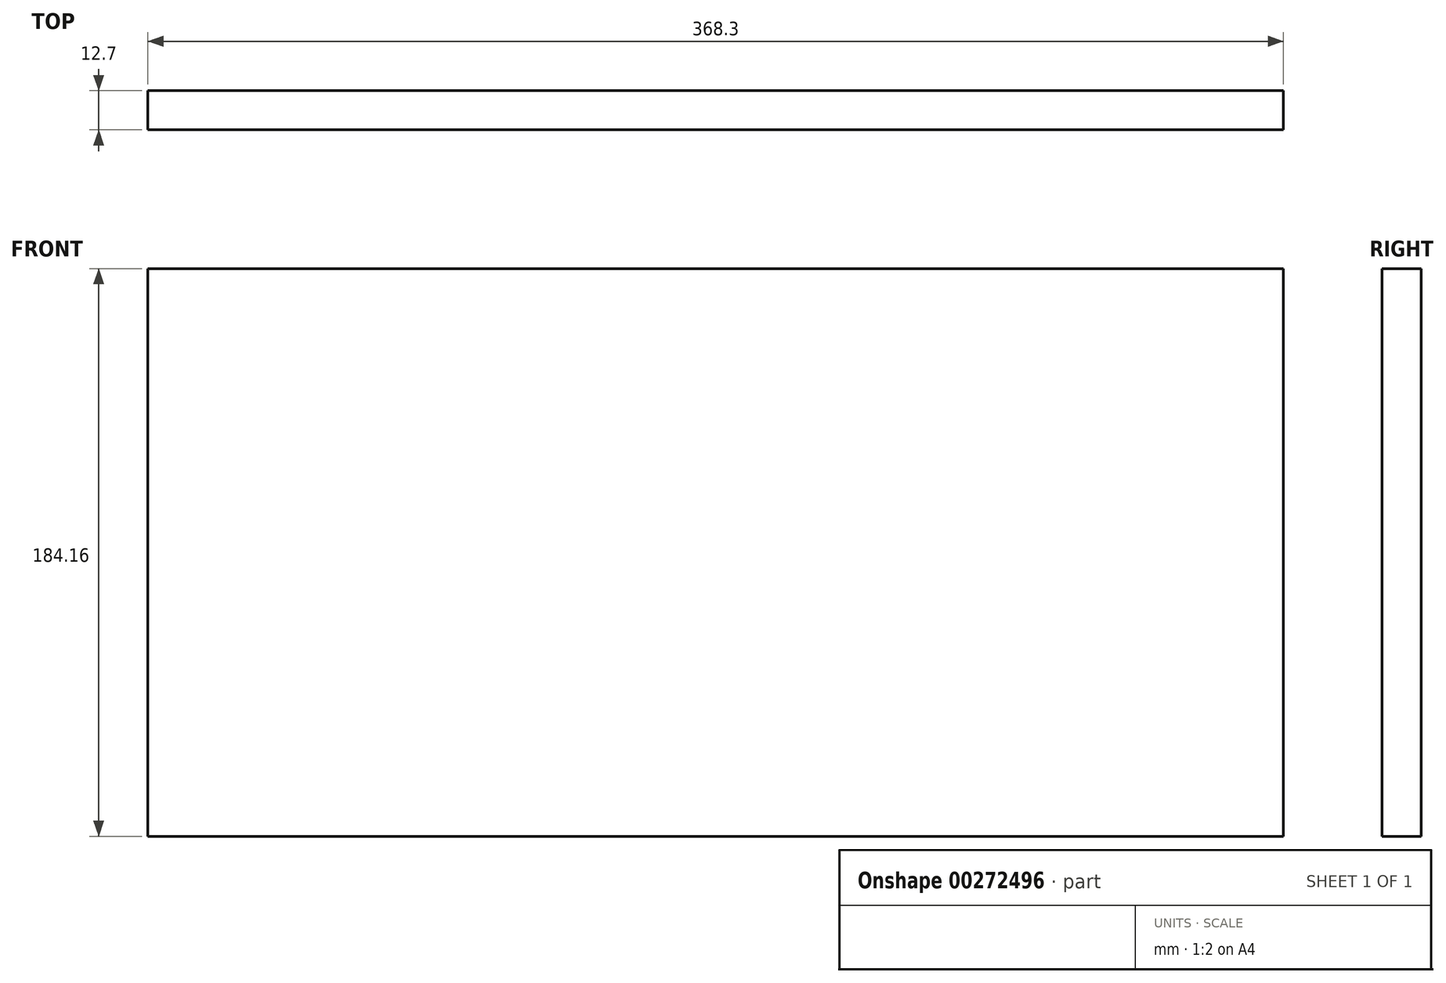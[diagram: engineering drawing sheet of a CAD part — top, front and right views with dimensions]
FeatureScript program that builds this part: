
annotation { "Feature Type Name" : "Feature", "Feature Type Description" : "" }
export const myFeature = defineFeature(function(context is Context, id is Id, definition is map)
    precondition{}
    {
        {
            var Q0;
            Q0=qCreatedBy(makeId("Front.planeOp"),FACE);
            var sketch = newSketch(context, id + "F0", { "sketchPlane" : qUnion([Q0])});
            skLineSegment(sketch, "E0.bottom", {"start": v(-184.15, 92.08) * mm, "end": v(184.15, 92.08) * mm});
            skLineSegment(sketch, "E0.top", {"start": v(-184.15, -92.07) * mm, "end": v(184.15, -92.07) * mm});
            skLineSegment(sketch, "E0.left", {"start": v(-184.15, 92.08) * mm, "end": v(-184.15, -92.07) * mm});
            skLineSegment(sketch, "E0.right", {"start": v(184.15, 92.08) * mm, "end": v(184.15, -92.07) * mm});
            skPoint(sketch, "E0.middle", {"position": v(0, 0) * mm});
            skSolve(sketch);
        }
        {
            var Q0;
            Q0=makeQuery(id+"F0.imprint","IMPRINT",FACE,{"disambiguationData":[TD([[makeQuery(id+"F0.imprint","IMPRINT",EDGE,{"derivedFrom":sQuery(id+"F0.wireOp",EDGE,"E0.bottom")}),-1.0]])]});
            extrude(context, id + "F1", {"entities" : qUnion([Q0]), "endBound" : BoundingType.SYMMETRIC, "depth" : 12.7 * mm, "offsetDistance" : 25.4 * mm});
        }
    });
